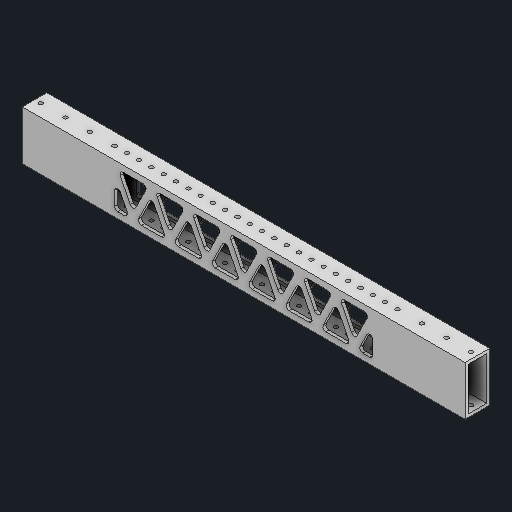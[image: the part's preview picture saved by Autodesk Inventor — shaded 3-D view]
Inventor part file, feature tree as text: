
AUTODESK INVENTOR PART (.ipt)
format: ipt  version: 2023 (Build 270158000, 158)  size: 420,352 bytes
history: native  units: in
note: dims shown in document units (in); Inventor stores cm internally (conversion verified against a paired STEP export)
features: sketch x5, other x3, plane x2
ambient origin geometry x8: Origin, YZ Plane, XZ Plane, XY Plane, X Axis, Y Axis, Z Axis, Center Point
bodies: Solid1 (feature_tree)
feature tree (10):
  other  "fram_extrusion_18in_MIR.ipt"
  other  "Solid1::fram_extrusion_18in_MIR.ipt"
  other  "TaggingFeature1"
  sketch  "Sketch1"  dims[d0=0.3937in]
  sketch  "Sketch2"
  sketch  "Sketch3"
  sketch  "Sketch4"
  sketch  "Sketch7"
  plane  "Work Plane1"
  plane  "Work Plane2"
